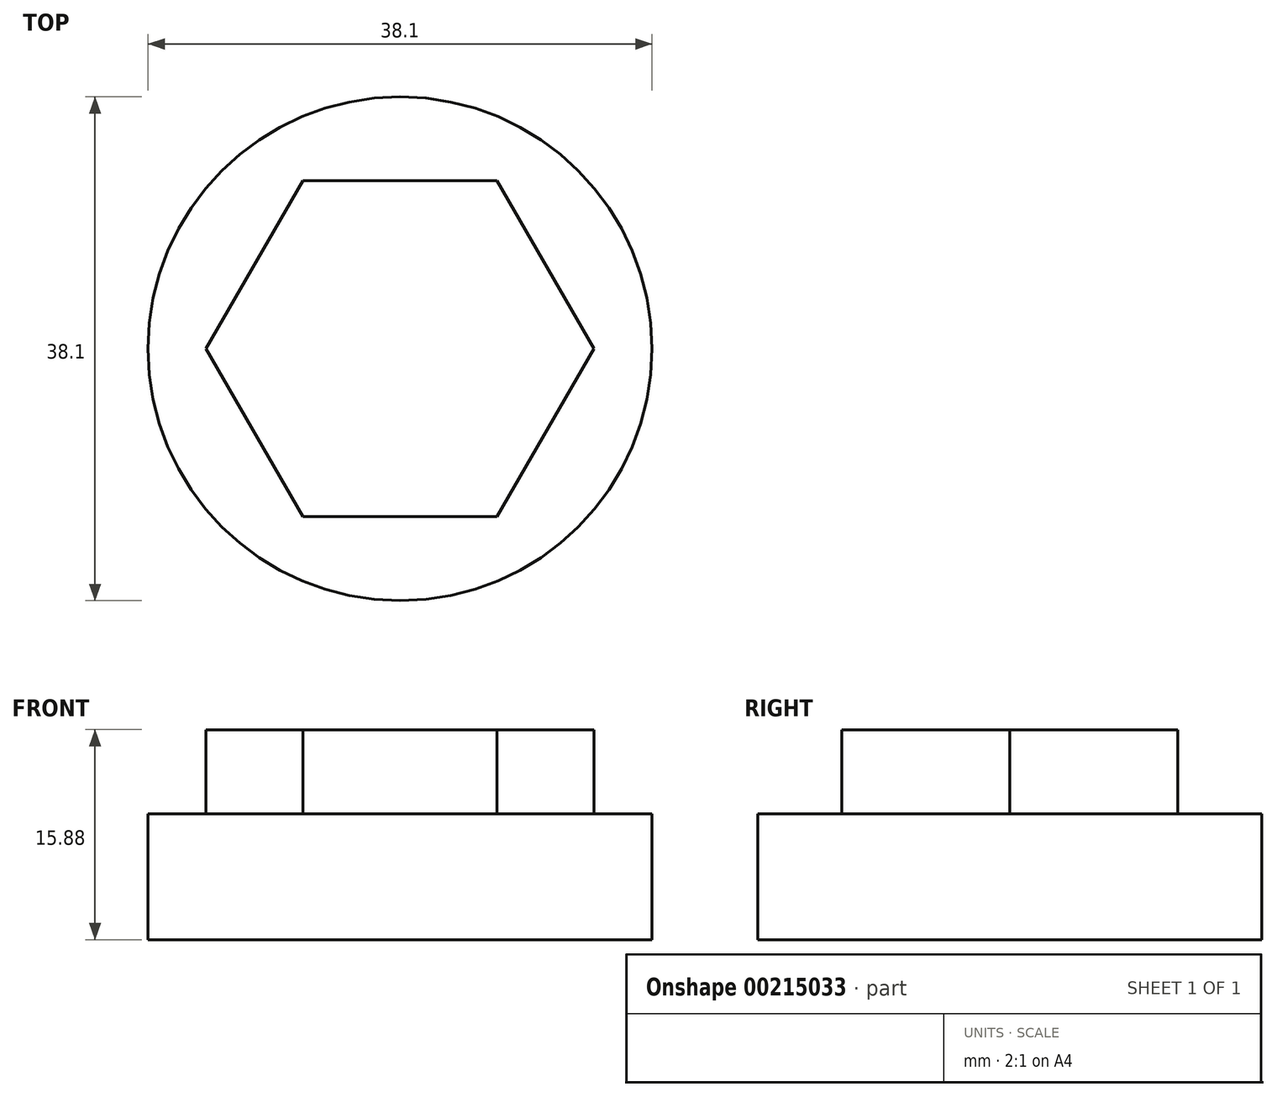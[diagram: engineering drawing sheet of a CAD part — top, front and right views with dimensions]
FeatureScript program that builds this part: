
annotation { "Feature Type Name" : "Feature", "Feature Type Description" : "" }
export const myFeature = defineFeature(function(context is Context, id is Id, definition is map)
    precondition{}
    {
        {
            var Q0;
            Q0=qCreatedBy(makeId("Top.planeOp"),FACE);
            var sketch = newSketch(context, id + "F0", { "sketchPlane" : qUnion([Q0])});
            skCircle(sketch, "E0", {"center": v(0, 0) * mm, "radius": 19.05 * mm});
            skSolve(sketch);
        }
        {
            var Q0;
            Q0 = qSketchRegion(id + "F0", true);
            extrude(context, id + "F1", {"entities" : qUnion([Q0]), "depth" : 9.52 * mm});
        }
        {
            var Q0;
            Q0=makeQuery(id+"F1.opExtrude","CAP_FACE",FACE,{"disambiguationData":[OSD([sQuery(id+"F0.wireOp",EDGE,"E0")])],"isStart":false});
            var sketch = newSketch(context, id + "F2", { "sketchPlane" : qUnion([Q0])});
            skCircle(sketch, "E1.cCircle", {"center": v(0, 0) * mm, "radius": 12.7 * mm, "construction": true});
            skLineSegment(sketch, "E1.0", {"start": v(-7.33, 12.7) * mm, "end": v(7.33, 12.7) * mm});
            skLineSegment(sketch, "E1.1", {"start": v(7.33, 12.7) * mm, "end": v(14.66, 0) * mm});
            skLineSegment(sketch, "E1.2", {"start": v(14.66, 0) * mm, "end": v(7.33, -12.7) * mm});
            skLineSegment(sketch, "E1.3", {"start": v(7.33, -12.7) * mm, "end": v(-7.33, -12.7) * mm});
            skLineSegment(sketch, "E1.4", {"start": v(-7.33, -12.7) * mm, "end": v(-14.66, 0) * mm});
            skLineSegment(sketch, "E1.5", {"start": v(-14.66, 0) * mm, "end": v(-7.33, 12.7) * mm});
            skPoint(sketch, "E1.0.midPoint", {"position": v(0, 12.7) * mm});
            skSolve(sketch);
        }
        {
            var Q0;
            Q0=makeQuery(id+"F2.imprint","IMPRINT",FACE,{"disambiguationData":[TD([[makeQuery(id+"F2.imprint","IMPRINT",EDGE,{"derivedFrom":sQuery(id+"F2.wireOp",EDGE,"E1.0")}),-1.0]])]});
            extrude(context, id + "F3", {"entities" : qUnion([Q0]), "operationType" : NewBodyOperationType.ADD, "depth" : 6.35 * mm});
        }
    });
